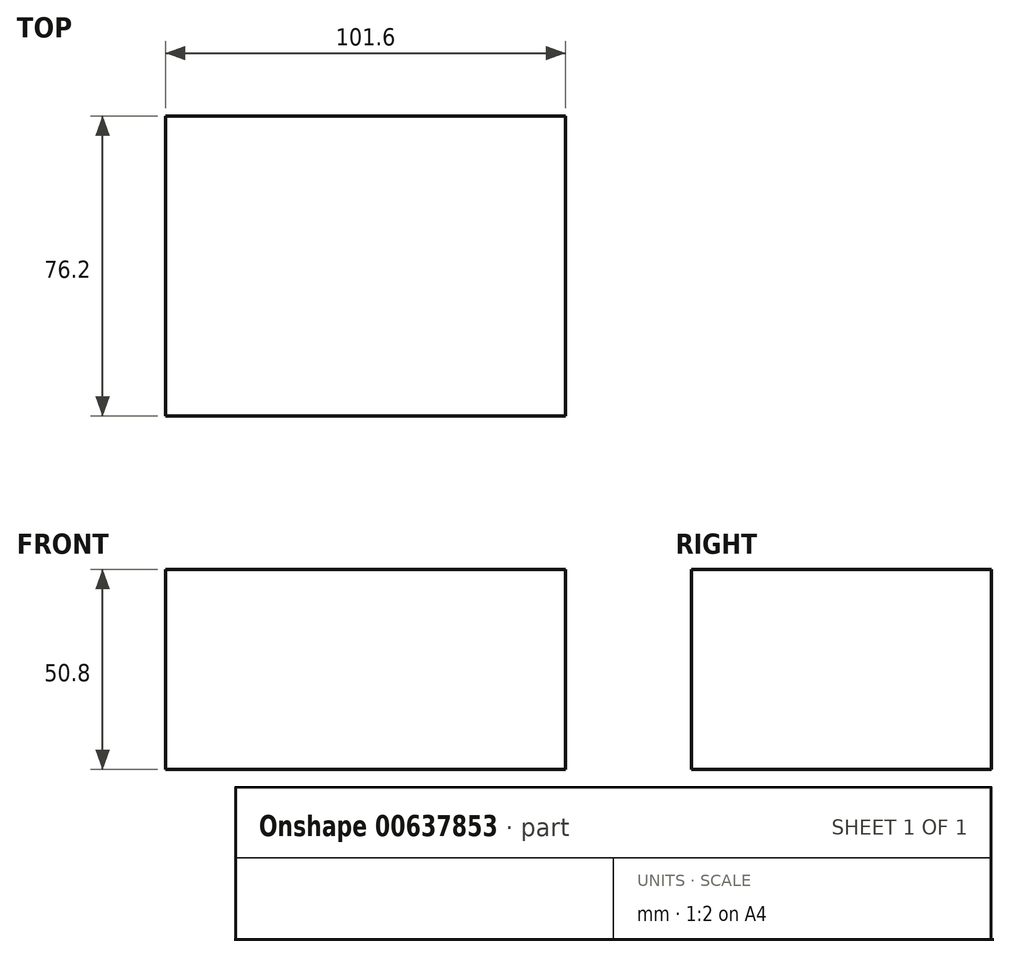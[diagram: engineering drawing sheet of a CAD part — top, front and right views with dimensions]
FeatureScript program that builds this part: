
annotation { "Feature Type Name" : "Feature", "Feature Type Description" : "" }
export const myFeature = defineFeature(function(context is Context, id is Id, definition is map)
    precondition{}
    {
        {
            var Q0;
            Q0=qCreatedBy(makeId("Front.planeOp"),FACE);
            var sketch = newSketch(context, id + "F0", { "sketchPlane" : qUnion([Q0])});
            skLineSegment(sketch, "E0.bottom", {"start": v(0, 0) * mm, "end": v(-101.6, 0) * mm});
            skLineSegment(sketch, "E0.top", {"start": v(0, 50.8) * mm, "end": v(-101.6, 50.8) * mm});
            skLineSegment(sketch, "E0.left", {"start": v(0, 0) * mm, "end": v(0, 50.8) * mm});
            skLineSegment(sketch, "E0.right", {"start": v(-101.6, 0) * mm, "end": v(-101.6, 50.8) * mm});
            skSolve(sketch);
        }
        {
            var Q0;
            Q0 = qSketchRegion(id + "F0", true);
            extrude(context, id + "F1", {"entities" : qUnion([Q0]), "depth" : 76.2 * mm, "offsetDistance" : 25.4 * mm});
        }
    });
